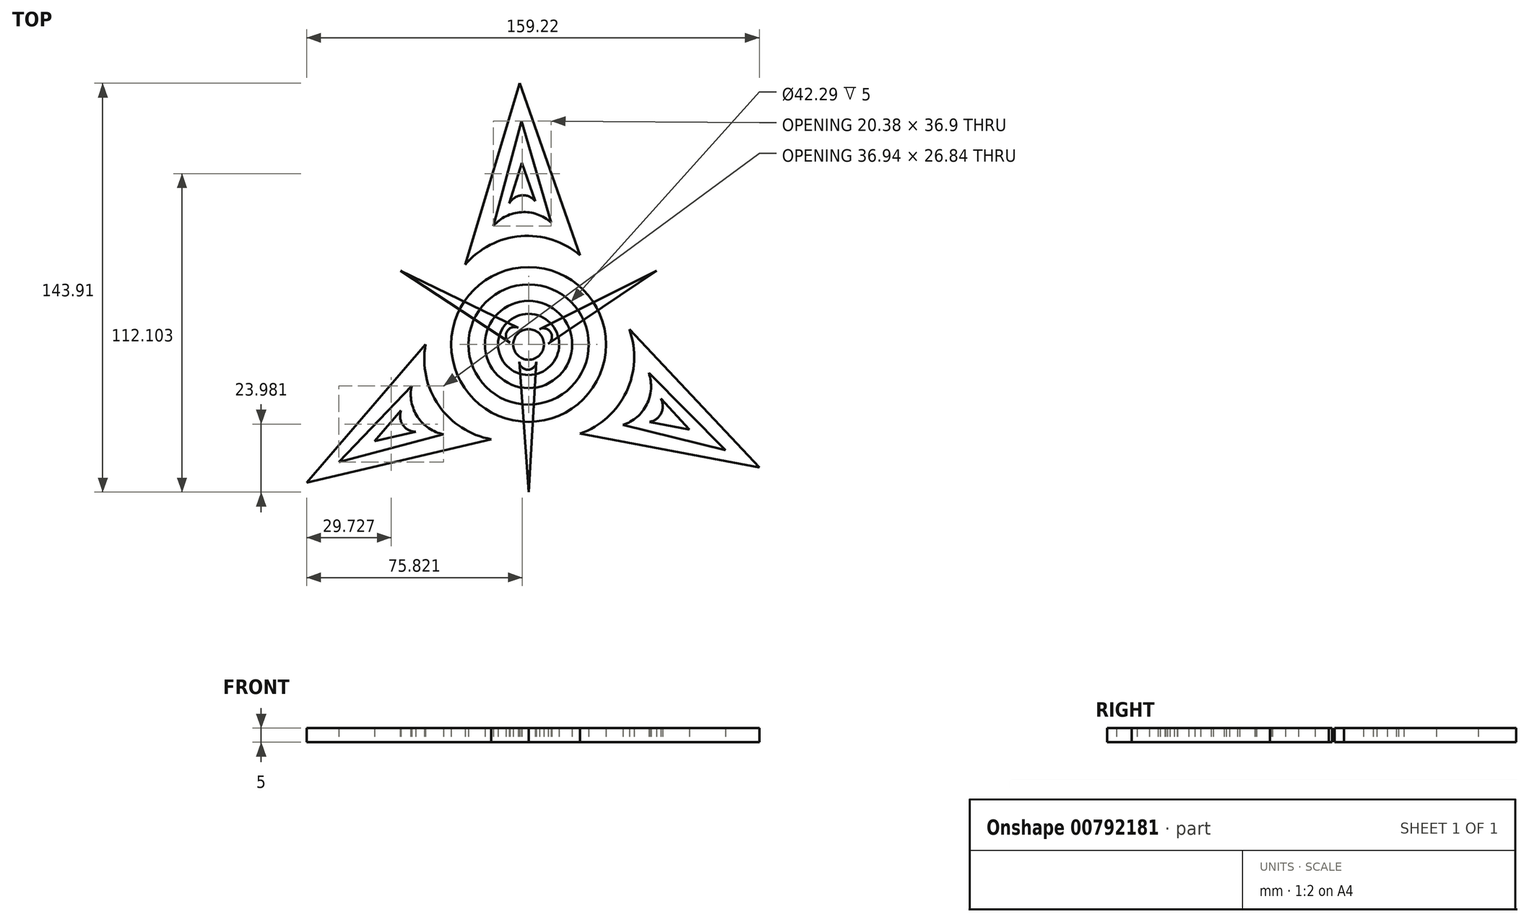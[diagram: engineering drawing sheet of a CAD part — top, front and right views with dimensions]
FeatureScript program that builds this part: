
annotation { "Feature Type Name" : "Feature", "Feature Type Description" : "" }
export const myFeature = defineFeature(function(context is Context, id is Id, definition is map)
    precondition{}
    {
        {
            var Q0;
            Q0=qCreatedBy(makeId("Top.planeOp"),FACE);
            var sketch = newSketch(context, id + "F0", { "sketchPlane" : qUnion([Q0])});
            skCircle(sketch, "E0", {"center": v(0, 0) * mm, "radius": 5.39 * mm});
            skCircle(sketch, "E1", {"center": v(0, 0) * mm, "radius": 10.75 * mm});
            skCircle(sketch, "E2", {"center": v(0, 0) * mm, "radius": 15.35 * mm});
            skCircle(sketch, "E3", {"center": v(0, 0) * mm, "radius": 21.14 * mm});
            skCircle(sketch, "E4", {"center": v(0, 0) * mm, "radius": 27.23 * mm});
            skArc(sketch, "E5", {"start": v(-36.22, 0) * mm, "mid": v(-31.61, -21.47) * mm, "end": v(-13.13, -33.34) * mm});
            skLineSegment(sketch, "E6", {"start": v(-36.22, 0) * mm, "end": v(-78.07, -48.63) * mm});
            skLineSegment(sketch, "E7", {"start": v(-13.13, -33.34) * mm, "end": v(-78.07, -48.63) * mm});
            skArc(sketch, "E8", {"start": v(-41.13, -14.58) * mm, "mid": v(-39.07, -25.45) * mm, "end": v(-29.87, -31.6) * mm});
            skLineSegment(sketch, "E9", {"start": v(-41.13, -14.58) * mm, "end": v(-66.81, -41.42) * mm});
            skLineSegment(sketch, "E10", {"start": v(-29.87, -31.6) * mm, "end": v(-66.81, -41.42) * mm});
            skArc(sketch, "E11", {"start": v(-44.88, -23.24) * mm, "mid": v(-44.23, -28.34) * mm, "end": v(-39.68, -30.74) * mm});
            skLineSegment(sketch, "E12", {"start": v(-44.88, -23.24) * mm, "end": v(-54.15, -34.01) * mm});
            skLineSegment(sketch, "E13", {"start": v(-54.15, -34.01) * mm, "end": v(-39.68, -30.74) * mm});
            skLineSegment(sketch, "E14.1.0", {"start": v(18.11, -31.37) * mm, "end": v(81.15, -43.3) * mm});
            skLineSegment(sketch, "E14.1.1", {"start": v(35.44, 5.3) * mm, "end": v(81.15, -43.3) * mm});
            skArc(sketch, "E14.1.2", {"start": v(18.11, -31.37) * mm, "mid": v(34.4, -16.64) * mm, "end": v(35.44, 5.3) * mm});
            skArc(sketch, "E14.1.3", {"start": v(33.19, -28.33) * mm, "mid": v(41.58, -21.1) * mm, "end": v(42.3, -10.07) * mm});
            skLineSegment(sketch, "E14.1.4", {"start": v(42.3, -10.07) * mm, "end": v(69.28, -37.15) * mm});
            skLineSegment(sketch, "E14.1.5", {"start": v(33.19, -28.33) * mm, "end": v(69.28, -37.15) * mm});
            skLineSegment(sketch, "E14.1.6", {"start": v(42.56, -27.25) * mm, "end": v(56.53, -29.9) * mm});
            skLineSegment(sketch, "E14.1.7", {"start": v(56.53, -29.9) * mm, "end": v(46.46, -19) * mm});
            skArc(sketch, "E14.1.8", {"start": v(42.56, -27.25) * mm, "mid": v(46.66, -24.14) * mm, "end": v(46.46, -19) * mm});
            skLineSegment(sketch, "E14.2.0", {"start": v(18.11, 31.37) * mm, "end": v(-3.08, 91.93) * mm});
            skLineSegment(sketch, "E14.2.1", {"start": v(-22.3, 28.04) * mm, "end": v(-3.08, 91.93) * mm});
            skArc(sketch, "E14.2.2", {"start": v(18.11, 31.37) * mm, "mid": v(-2.79, 38.11) * mm, "end": v(-22.3, 28.04) * mm});
            skArc(sketch, "E14.2.3", {"start": v(7.94, 42.9) * mm, "mid": v(-2.5, 46.56) * mm, "end": v(-12.44, 41.67) * mm});
            skLineSegment(sketch, "E14.2.4", {"start": v(-12.44, 41.67) * mm, "end": v(-2.46, 78.57) * mm});
            skLineSegment(sketch, "E14.2.5", {"start": v(7.94, 42.9) * mm, "end": v(-2.46, 78.57) * mm});
            skLineSegment(sketch, "E14.2.6", {"start": v(2.32, 50.49) * mm, "end": v(-2.38, 63.9) * mm});
            skLineSegment(sketch, "E14.2.7", {"start": v(-2.38, 63.9) * mm, "end": v(-6.78, 49.74) * mm});
            skArc(sketch, "E14.2.8", {"start": v(2.32, 50.49) * mm, "mid": v(-2.43, 52.47) * mm, "end": v(-6.78, 49.74) * mm});
            skSolve(sketch);
        }
        {
            var Q0;
            Q0=qCreatedBy(makeId("Top.planeOp"),FACE);
            var sketch = newSketch(context, id + "F1", { "sketchPlane" : qUnion([Q0])});
            skLineSegment(sketch, "E15", {"start": v(-3.26, -6.1) * mm, "end": v(0, -51.98) * mm});
            skLineSegment(sketch, "E16", {"start": v(0, -51.98) * mm, "end": v(2.74, -6.06) * mm});
            skArc(sketch, "E17", {"start": v(-3.26, -6.1) * mm, "mid": v(-0.24, -8.89) * mm, "end": v(2.74, -6.06) * mm});
            skLineSegment(sketch, "E18.1.0", {"start": v(6.9, 0.23) * mm, "end": v(45.01, 25.99) * mm});
            skLineSegment(sketch, "E18.1.1", {"start": v(45.01, 25.99) * mm, "end": v(3.88, 5.4) * mm});
            skArc(sketch, "E18.1.2", {"start": v(6.9, 0.23) * mm, "mid": v(7.82, 4.23) * mm, "end": v(3.88, 5.4) * mm});
            skLineSegment(sketch, "E18.2.0", {"start": v(-3.65, 5.87) * mm, "end": v(-45.01, 25.99) * mm});
            skLineSegment(sketch, "E18.2.1", {"start": v(-45.01, 25.99) * mm, "end": v(-6.62, 0.65) * mm});
            skArc(sketch, "E18.2.2", {"start": v(-3.65, 5.87) * mm, "mid": v(-7.58, 4.65) * mm, "end": v(-6.62, 0.65) * mm});
            skPoint(sketch, "E18.center", {"position": v(0, 0) * mm});
            skSolve(sketch);
        }
        {
            var Q0;
            Q0=makeQuery(id+"F1.imprint","IMPRINT",FACE,{"disambiguationData":[TD([[makeQuery(id+"F1.imprint","IMPRINT",EDGE,{"derivedFrom":sQuery(id+"F1.wireOp",EDGE,"E18.2.0")}),1.0]])]});
            var Q1;
            Q1=makeQuery(id+"F1.imprint","IMPRINT",FACE,{"disambiguationData":[TD([[makeQuery(id+"F1.imprint","IMPRINT",EDGE,{"derivedFrom":sQuery(id+"F1.wireOp",EDGE,"E15")}),1.0]])]});
            var Q2;
            Q2=makeQuery(id+"F1.imprint","IMPRINT",FACE,{"disambiguationData":[TD([[makeQuery(id+"F1.imprint","IMPRINT",EDGE,{"derivedFrom":sQuery(id+"F1.wireOp",EDGE,"E18.1.0")}),1.0]])]});
            extrude(context, id + "F2", {"entities" : qUnion([Q0, Q1, Q2]), "depth" : 5 * mm, "offsetDistance" : 25 * mm});
        }
        {
            var Q0;
            Q0=makeQuery(id+"F0.imprint","IMPRINT",FACE,{"disambiguationData":[TD([[makeQuery(id+"F0.imprint","IMPRINT",EDGE,{"derivedFrom":sQuery(id+"F0.wireOp",EDGE,"E0")}),1.0]])]});
            var Q1;
            Q1=makeQuery(id+"F0.imprint","IMPRINT",FACE,{"disambiguationData":[TD([[makeQuery(id+"F0.imprint","IMPRINT",EDGE,{"derivedFrom":sQuery(id+"F0.wireOp",EDGE,"E1")}),-1.0]])]});
            var Q2;
            Q2=makeQuery(id+"F0.imprint","IMPRINT",FACE,{"disambiguationData":[TD([[makeQuery(id+"F0.imprint","IMPRINT",EDGE,{"derivedFrom":sQuery(id+"F0.wireOp",EDGE,"E3")}),-1.0]])]});
            var Q3;
            Q3=makeQuery(id+"F0.imprint","IMPRINT",FACE,{"disambiguationData":[TD([[makeQuery(id+"F0.imprint","IMPRINT",EDGE,{"derivedFrom":sQuery(id+"F0.wireOp",EDGE,"E5")}),-1.0]])]});
            var Q4;
            Q4=makeQuery(id+"F0.imprint","IMPRINT",FACE,{"disambiguationData":[TD([[makeQuery(id+"F0.imprint","IMPRINT",EDGE,{"derivedFrom":sQuery(id+"F0.wireOp",EDGE,"E11")}),-1.0]])]});
            var Q5;
            Q5=makeQuery(id+"F0.imprint","IMPRINT",FACE,{"disambiguationData":[TD([[makeQuery(id+"F0.imprint","IMPRINT",EDGE,{"derivedFrom":sQuery(id+"F0.wireOp",EDGE,"E14.2.0")}),1.0]])]});
            var Q6;
            Q6=makeQuery(id+"F0.imprint","IMPRINT",FACE,{"disambiguationData":[TD([[makeQuery(id+"F0.imprint","IMPRINT",EDGE,{"derivedFrom":sQuery(id+"F0.wireOp",EDGE,"E14.2.6")}),1.0]])]});
            var Q7;
            Q7=makeQuery(id+"F0.imprint","IMPRINT",FACE,{"disambiguationData":[TD([[makeQuery(id+"F0.imprint","IMPRINT",EDGE,{"derivedFrom":sQuery(id+"F0.wireOp",EDGE,"E14.1.0")}),1.0]])]});
            var Q8;
            Q8=makeQuery(id+"F0.imprint","IMPRINT",FACE,{"disambiguationData":[TD([[makeQuery(id+"F0.imprint","IMPRINT",EDGE,{"derivedFrom":sQuery(id+"F0.wireOp",EDGE,"E14.1.6")}),1.0]])]});
            extrude(context, id + "F3", {"entities" : qUnion([Q0, Q1, Q2, Q3, Q4, Q5, Q6, Q7, Q8]), "depth" : 5 * mm, "offsetDistance" : 25 * mm});
        }
    });
